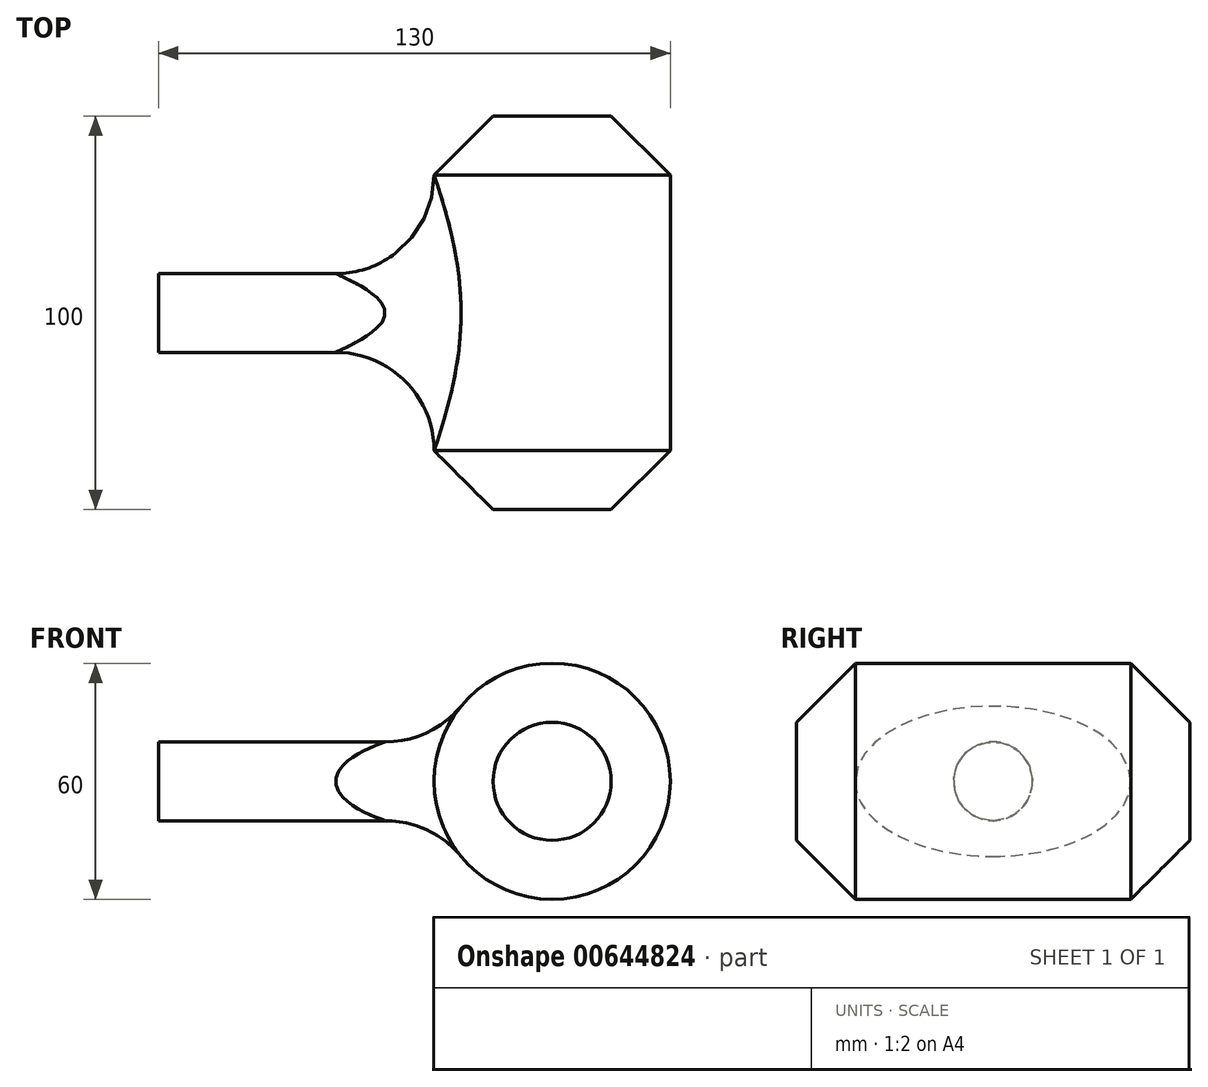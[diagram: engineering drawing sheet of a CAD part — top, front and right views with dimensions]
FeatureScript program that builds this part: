
annotation { "Feature Type Name" : "Feature", "Feature Type Description" : "" }
export const myFeature = defineFeature(function(context is Context, id is Id, definition is map)
    precondition{}
    {
        {
            var Q0;
            Q0=qCreatedBy(makeId("Front.planeOp"),FACE);
            var sketch = newSketch(context, id + "F0", { "sketchPlane" : qUnion([Q0])});
            skCircle(sketch, "E0", {"center": v(0, 0) * mm, "radius": 30 * mm});
            skSolve(sketch);
        }
        {
            var Q0;
            Q0 = qSketchRegion(id + "F0", true);
            extrude(context, id + "F1", {"entities" : qUnion([Q0]), "endBound" : BoundingType.SYMMETRIC, "depth" : 100 * mm, "offsetDistance" : 25 * mm});
        }
        {
            var Q0;
            Q0=qCreatedBy(makeId("Right.planeOp"),FACE);
            var sketch = newSketch(context, id + "F2", { "sketchPlane" : qUnion([Q0])});
            skCircle(sketch, "E1", {"center": v(0, 0) * mm, "radius": 10 * mm});
            skSolve(sketch);
        }
        {
            var Q0;
            Q0 = qSketchRegion(id + "F2", true);
            extrude(context, id + "F3", {"entities" : qUnion([Q0]), "operationType" : NewBodyOperationType.ADD, "oppositeDirection" : true, "depth" : 100 * mm, "offsetDistance" : 25 * mm});
        }
        {
            var Q0;
            Q0=makeQuery(id+"F3.boolean.opBoolean","INTERSECT",EDGE,{"derivedFrom":[makeQuery(id+"F1.opExtrude","SWEPT_FACE",FACE,{"disambiguationData":[OSD([sQuery(id+"F0.wireOp",EDGE,"E0")])]}),makeQuery(id+"F3.opExtrude","SWEPT_FACE",FACE,{"disambiguationData":[OSD([sQuery(id+"F2.wireOp",EDGE,"E1")])]})]});
            fillet(context, id + "F4", {"entities" : qUnion([Q0]), "radius" : 25 * mm, "tangentPropagation" : true, "allowEdgeOverflow" : false});
        }
        {
            var Q0;
            Q0=makeQuery(id+"F1.opExtrude","CAP_EDGE",EDGE,{"disambiguationData":[OSD([sQuery(id+"F0.wireOp",EDGE,"E0")])],"isStart":false});
            var Q1;
            Q1=makeQuery(id+"F1.opExtrude","CAP_EDGE",EDGE,{"disambiguationData":[OSD([sQuery(id+"F0.wireOp",EDGE,"E0")])],"isStart":true});
            chamfer(context, id + "F5", {"entities" : qUnion([Q0, Q1]), "width" : 15 * mm, "tangentPropagation" : true});
        }
    });
